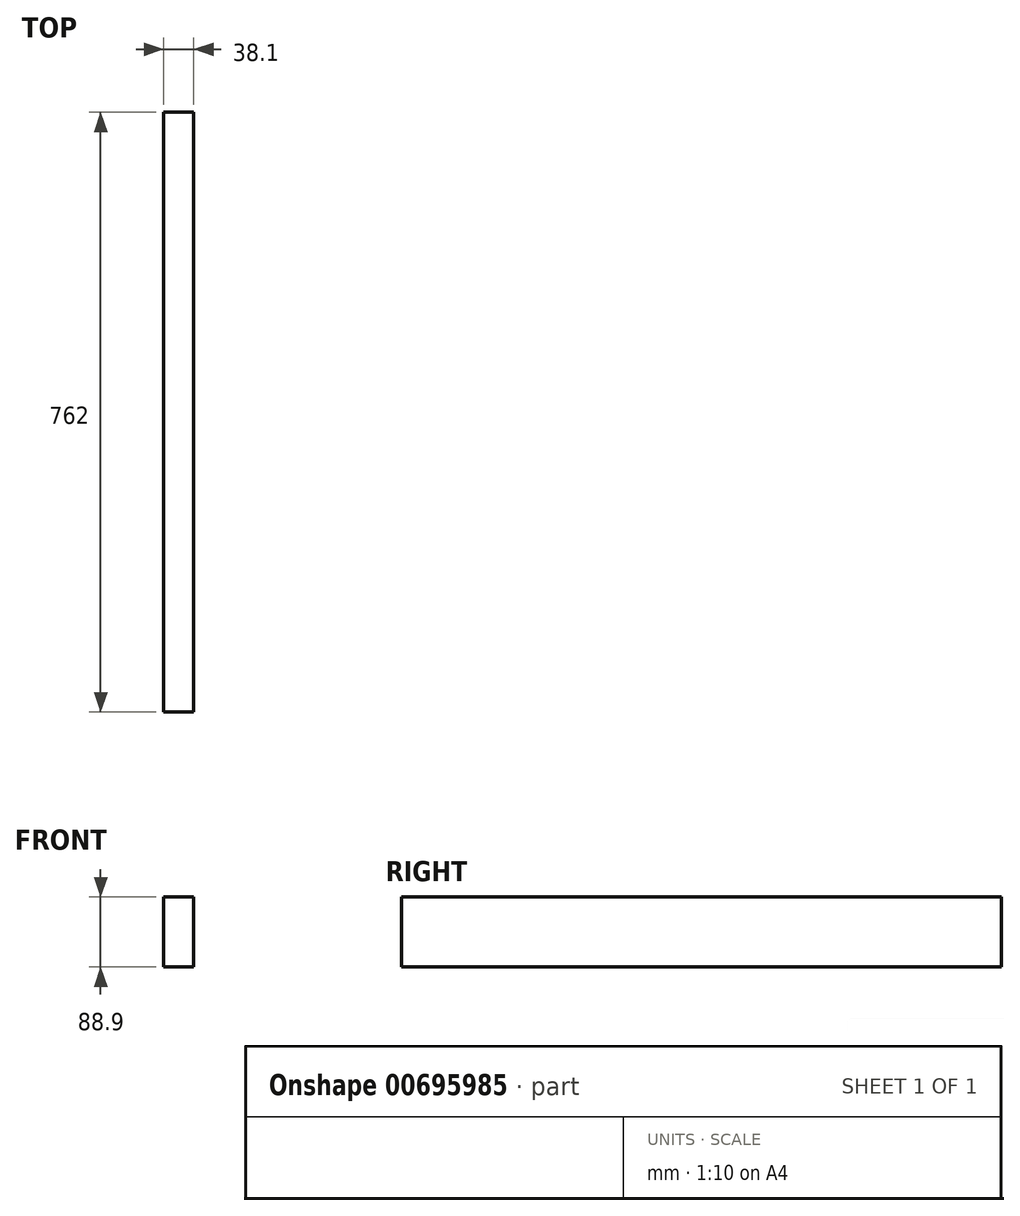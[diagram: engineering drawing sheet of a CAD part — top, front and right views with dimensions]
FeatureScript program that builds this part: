
annotation { "Feature Type Name" : "Feature", "Feature Type Description" : "" }
export const myFeature = defineFeature(function(context is Context, id is Id, definition is map)
    precondition{}
    {
        {
            var Q0;
            Q0=qCreatedBy(makeId("Right.planeOp"),FACE);
            var sketch = newSketch(context, id + "F0", { "sketchPlane" : qUnion([Q0])});
            skLineSegment(sketch, "E0.bottom", {"start": v(0, 0) * mm, "end": v(-762, 0) * mm});
            skLineSegment(sketch, "E0.top", {"start": v(0, 88.9) * mm, "end": v(-762, 88.9) * mm});
            skLineSegment(sketch, "E0.left", {"start": v(0, 0) * mm, "end": v(0, 88.9) * mm});
            skLineSegment(sketch, "E0.right", {"start": v(-762, 0) * mm, "end": v(-762, 88.9) * mm});
            skSolve(sketch);
        }
        {
            var Q0;
            Q0=makeQuery(id+"F0.imprint","IMPRINT",FACE,{"disambiguationData":[TD([[makeQuery(id+"F0.imprint","IMPRINT",EDGE,{"derivedFrom":sQuery(id+"F0.wireOp",EDGE,"E0.bottom")}),-1.0]])]});
            extrude(context, id + "F1", {"entities" : qUnion([Q0]), "depth" : 38.1 * mm, "offsetDistance" : 25.4 * mm});
        }
    });
